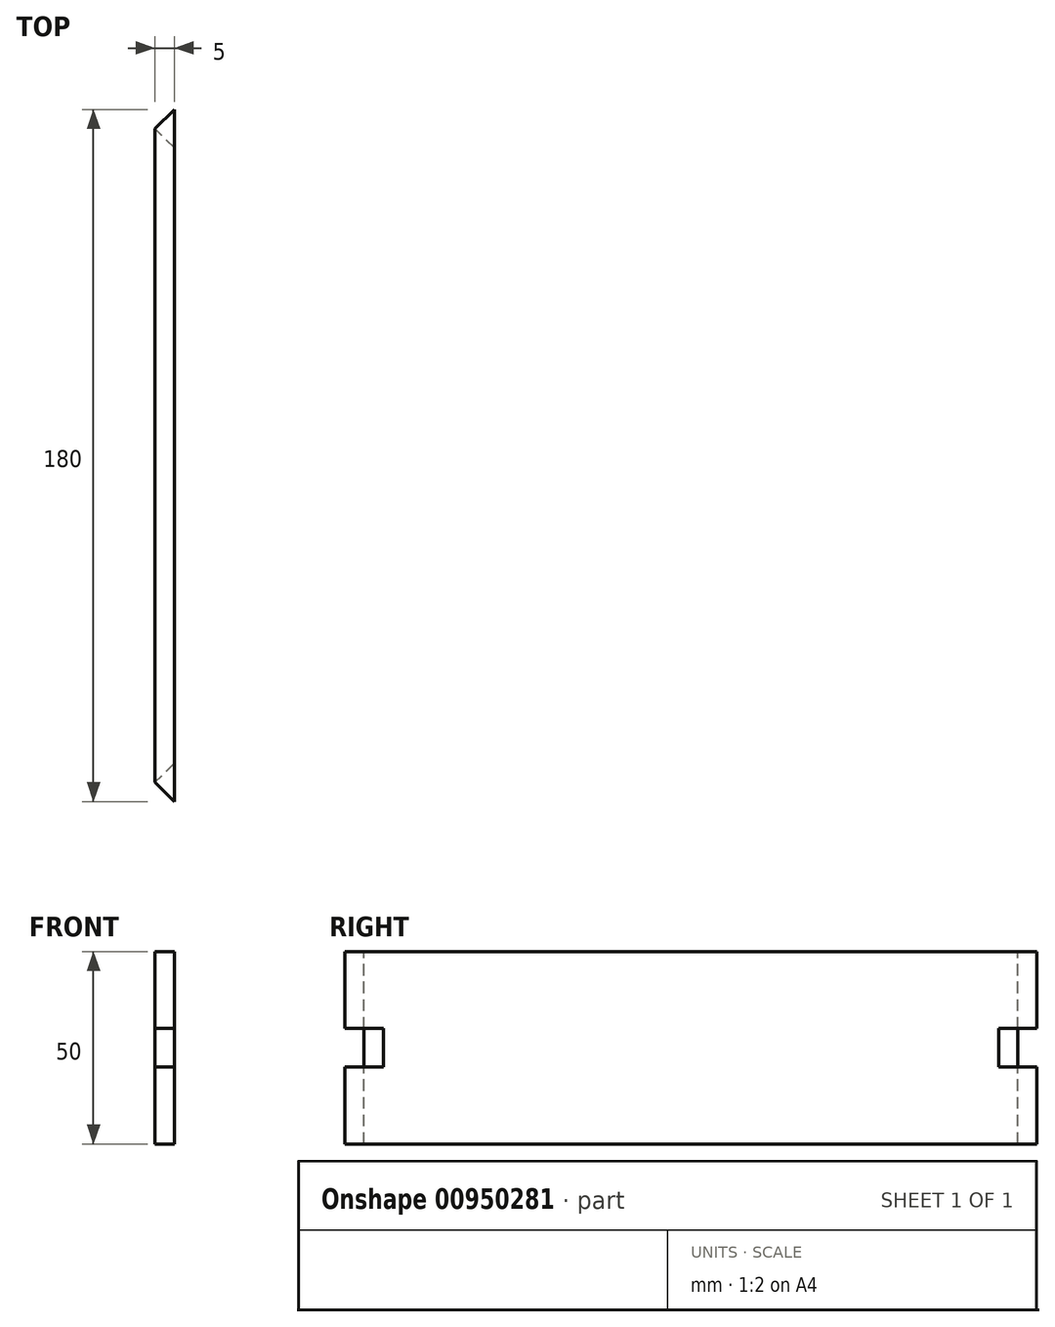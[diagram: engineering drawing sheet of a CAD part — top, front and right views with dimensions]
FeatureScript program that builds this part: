
annotation { "Feature Type Name" : "Feature", "Feature Type Description" : "" }
export const myFeature = defineFeature(function(context is Context, id is Id, definition is map)
    precondition{}
    {
        {
            var Q0;
            Q0=qCreatedBy(makeId("Right.planeOp"),FACE);
            var sketch = newSketch(context, id + "F0", { "sketchPlane" : qUnion([Q0])});
            skPoint(sketch, "E0.middle", {"position": v(0, 0) * mm});
            skLineSegment(sketch, "E1.bottom", {"start": v(90, -25) * mm, "end": v(-90, -25) * mm});
            skLineSegment(sketch, "E1.top", {"start": v(90, 25) * mm, "end": v(-90, 25) * mm});
            skLineSegment(sketch, "E1.left", {"start": v(90, -25) * mm, "end": v(90, 25) * mm});
            skLineSegment(sketch, "E1.right", {"start": v(-90, -25) * mm, "end": v(-90, 25) * mm});
            skSolve(sketch);
        }
        {
            var Q0;
            Q0=makeQuery(id+"F0.imprint","IMPRINT",FACE,{"disambiguationData":[TD([[makeQuery(id+"F0.imprint","IMPRINT",EDGE,{"derivedFrom":sQuery(id+"F0.wireOp",EDGE,"E1.bottom")}),-1.0]])]});
            extrude(context, id + "F1", {"entities" : qUnion([Q0]), "endBound" : BoundingType.SYMMETRIC, "depth" : 5 * mm, "offsetDistance" : 25 * mm});
        }
        {
            var Q0;
            Q0=makeQuery(id+"F1.opExtrude","SWEPT_FACE",FACE,{"disambiguationData":[OSD([sQuery(id+"F0.wireOp",EDGE,"E1.top")])]});
            var sketch = newSketch(context, id + "F2", { "sketchPlane" : qUnion([Q0])});
            skLineSegment(sketch, "E2", {"start": v(-2.5, -90) * mm, "end": v(2.5, -90) * mm});
            skLineSegment(sketch, "E3", {"start": v(-2.5, -90) * mm, "end": v(-2.5, -85) * mm});
            skLineSegment(sketch, "E4", {"start": v(-2.5, -85) * mm, "end": v(2.5, -90) * mm});
            skSolve(sketch);
        }
        {
            var Q0;
            Q0=makeQuery(id+"F2.imprint","IMPRINT",FACE,{"disambiguationData":[TD([[makeQuery(id+"F2.imprint","IMPRINT",EDGE,{"derivedFrom":sQuery(id+"F2.wireOp",EDGE,"E2")}),-1.0]])]});
            extrude(context, id + "F3", {"entities" : qUnion([Q0]), "operationType" : NewBodyOperationType.REMOVE, "oppositeDirection" : true, "depth" : 60 * mm, "offsetDistance" : 25 * mm});
        }
        {
            var Q0;
            Q0=makeQuery(id+"F1.opExtrude","SWEPT_FACE",FACE,{"disambiguationData":[OSD([sQuery(id+"F0.wireOp",EDGE,"E1.top")])]});
            var sketch = newSketch(context, id + "F4", { "sketchPlane" : qUnion([Q0])});
            skLineSegment(sketch, "E5", {"start": v(-2.5, 90) * mm, "end": v(2.5, 90) * mm});
            skLineSegment(sketch, "E6", {"start": v(-2.5, 90) * mm, "end": v(-2.5, 85) * mm});
            skLineSegment(sketch, "E7", {"start": v(-2.5, 85) * mm, "end": v(2.5, 90) * mm});
            skSolve(sketch);
        }
        {
            var Q0;
            Q0=makeQuery(id+"F4.imprint","IMPRINT",FACE,{"disambiguationData":[TD([[makeQuery(id+"F4.imprint","IMPRINT",EDGE,{"derivedFrom":sQuery(id+"F4.wireOp",EDGE,"E5")}),1.0]])]});
            extrude(context, id + "F5", {"entities" : qUnion([Q0]), "operationType" : NewBodyOperationType.REMOVE, "oppositeDirection" : true, "depth" : 50 * mm, "offsetDistance" : 25 * mm});
        }
        {
            var Q0;
            Q0=makeQuery(id+"F3.boolean.opBoolean","COPY",FACE,{"derivedFrom":makeQuery(id+"F3.opExtrude","SWEPT_FACE",FACE,{"disambiguationData":[OSD([sQuery(id+"F2.wireOp",EDGE,"E4")])]})});
            var sketch = newSketch(context, id + "F6", { "sketchPlane" : qUnion([Q0])});
            skLineSegment(sketch, "E8", {"start": v(65.4, 0) * mm, "end": v(58.34, 0) * mm});
            skLineSegment(sketch, "E9.bottom", {"start": v(65.4, -5) * mm, "end": v(58.34, -5) * mm});
            skLineSegment(sketch, "E9.top", {"start": v(65.4, 5) * mm, "end": v(58.34, 5) * mm});
            skLineSegment(sketch, "E9.left", {"start": v(65.4, -5) * mm, "end": v(65.4, 5) * mm});
            skLineSegment(sketch, "E9.right", {"start": v(58.34, -5) * mm, "end": v(58.34, 5) * mm});
            skPoint(sketch, "E9.middle", {"position": v(61.87, 0) * mm});
            skSolve(sketch);
        }
        {
            var Q0;
            Q0 = qSketchRegion(id + "F6", true);
            extrude(context, id + "F7", {"entities" : qUnion([Q0]), "operationType" : NewBodyOperationType.REMOVE, "oppositeDirection" : true, "depth" : 25 * mm, "offsetDistance" : 25 * mm});
        }
        {
            var Q0;
            Q0=makeQuery(id+"F5.boolean.opBoolean","COPY",FACE,{"derivedFrom":makeQuery(id+"F5.opExtrude","SWEPT_FACE",FACE,{"disambiguationData":[OSD([sQuery(id+"F4.wireOp",EDGE,"E7")])]})});
            var sketch = newSketch(context, id + "F8", { "sketchPlane" : qUnion([Q0])});
            skLineSegment(sketch, "E10", {"start": v(-58.34, 0) * mm, "end": v(-65.4, 0) * mm});
            skLineSegment(sketch, "E11.bottom", {"start": v(-58.34, -5) * mm, "end": v(-65.4, -5) * mm});
            skLineSegment(sketch, "E11.top", {"start": v(-58.34, 5) * mm, "end": v(-65.4, 5) * mm});
            skLineSegment(sketch, "E11.left", {"start": v(-58.34, -5) * mm, "end": v(-58.34, 5) * mm});
            skLineSegment(sketch, "E11.right", {"start": v(-65.4, -5) * mm, "end": v(-65.4, 5) * mm});
            skPoint(sketch, "E11.middle", {"position": v(-61.87, 0) * mm});
            skSolve(sketch);
        }
        {
            var Q0;
            Q0 = qSketchRegion(id + "F8", true);
            extrude(context, id + "F9", {"entities" : qUnion([Q0]), "operationType" : NewBodyOperationType.REMOVE, "oppositeDirection" : true, "depth" : 25 * mm, "offsetDistance" : 25 * mm});
        }
    });
